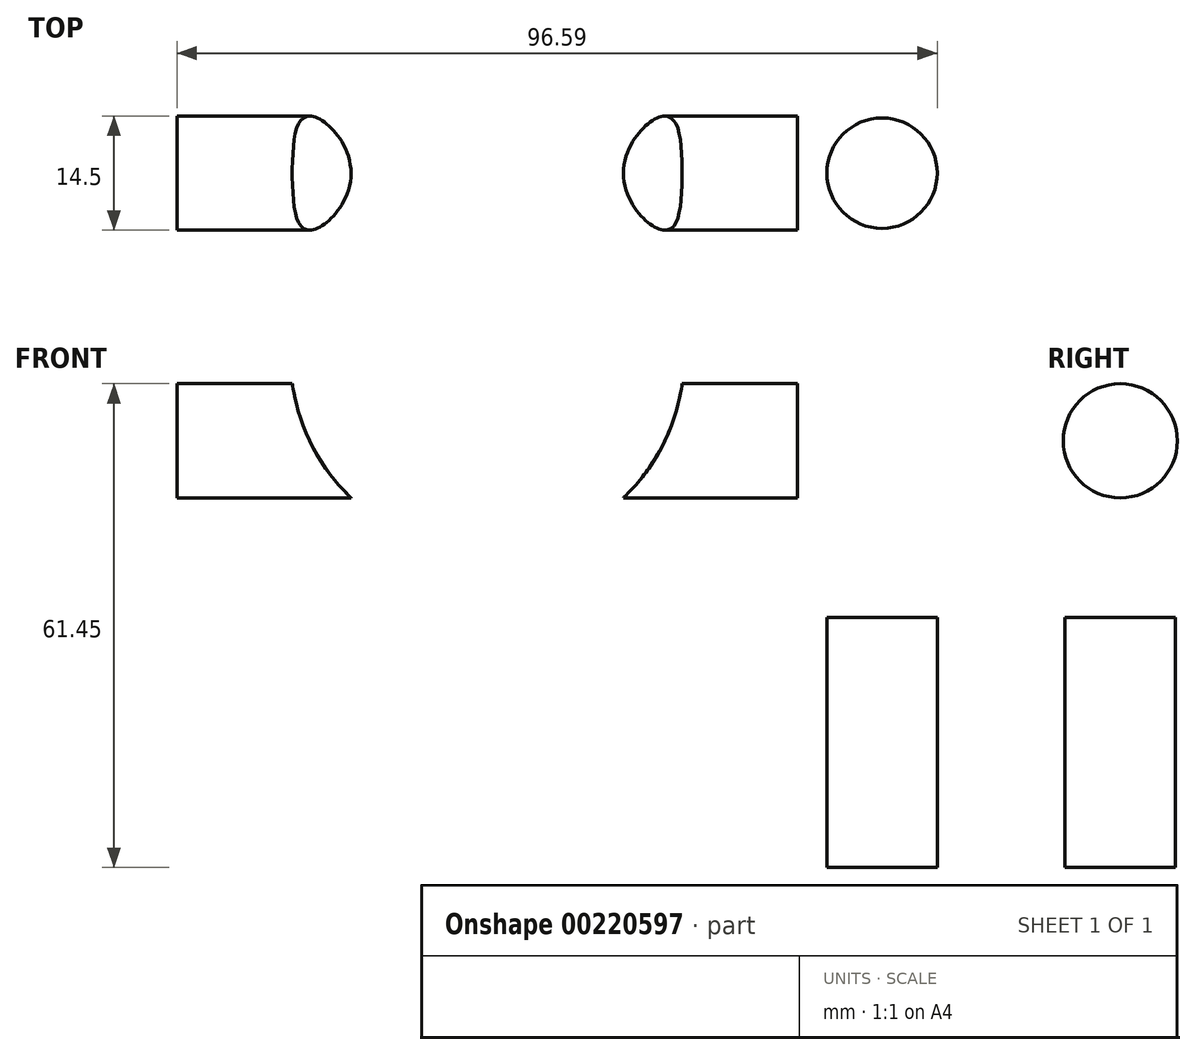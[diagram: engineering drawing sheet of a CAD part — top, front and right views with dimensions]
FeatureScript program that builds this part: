
annotation { "Feature Type Name" : "Feature", "Feature Type Description" : "" }
export const myFeature = defineFeature(function(context is Context, id is Id, definition is map)
    precondition{}
    {
        {
            var Q0;
            Q0=qCreatedBy(makeId("Top.planeOp"),FACE);
            var sketch = newSketch(context, id + "F0", { "sketchPlane" : qUnion([Q0])});
            skLineSegment(sketch, "E0.bottom", {"start": v(-41.16, 20.3) * mm, "end": v(41.16, 20.3) * mm});
            skLineSegment(sketch, "E0.top", {"start": v(-41.16, -20.3) * mm, "end": v(41.16, -20.3) * mm});
            skLineSegment(sketch, "E0.left", {"start": v(-41.16, 20.3) * mm, "end": v(-41.16, -20.3) * mm});
            skLineSegment(sketch, "E0.right", {"start": v(41.16, 20.3) * mm, "end": v(41.16, -20.3) * mm});
            skPoint(sketch, "E0.middle", {"position": v(0, 0) * mm});
            skCircle(sketch, "E1", {"center": v(-41.16, 0) * mm, "radius": 20.36 * mm});
            skCircle(sketch, "E2", {"center": v(41.16, 0) * mm, "radius": 20.35 * mm});
            skSolve(sketch);
        }
        {
            var Q0;
            {var subQ0=sQuery(id+"F0.wireOp",EDGE,"E1");var subQ1=sQuery(id+"F0.wireOp",EDGE,"E0.bottom");var subQ2=makeQuery(id+"F0.imprint","INTERSECT",VERTEX,{"derivedFrom":[subQ1,subQ0]});Q0=makeQuery(id+"F0.imprint","IMPRINT",FACE,{"disambiguationData":[TD([[makeQuery(id+"F0.imprint","IMPRINT",EDGE,{"disambiguationData":[TD([[subQ2,-1.0]])],"derivedFrom":subQ1}),-1.0]])]});}
            var Q1;
            {var subQ0=sQuery(id+"F0.wireOp",EDGE,"E0.left");Q1=makeQuery(id+"F0.imprint","IMPRINT",FACE,{"disambiguationData":[TD([[makeQuery(id+"F0.imprint","IMPRINT",EDGE,{"derivedFrom":subQ0}),1.0]])]});}
            var Q2;
            {var subQ0=sQuery(id+"F0.wireOp",EDGE,"E0.left");Q2=makeQuery(id+"F0.imprint","IMPRINT",FACE,{"disambiguationData":[TD([[makeQuery(id+"F0.imprint","IMPRINT",EDGE,{"derivedFrom":subQ0}),-1.0]])]});}
            var Q3;
            {var subQ0=sQuery(id+"F0.wireOp",EDGE,"E0.right");Q3=makeQuery(id+"F0.imprint","IMPRINT",FACE,{"disambiguationData":[TD([[makeQuery(id+"F0.imprint","IMPRINT",EDGE,{"derivedFrom":subQ0}),-1.0]])]});}
            var Q4;
            {var subQ0=sQuery(id+"F0.wireOp",EDGE,"E0.right");Q4=makeQuery(id+"F0.imprint","IMPRINT",FACE,{"disambiguationData":[TD([[makeQuery(id+"F0.imprint","IMPRINT",EDGE,{"derivedFrom":subQ0}),1.0]])]});}
            extrude(context, id + "F1", {"entities" : qUnion([Q0, Q1, Q2, Q3, Q4]), "depth" : 31.75 * mm});
        }
        {
            var Q0;
            Q0=makeQuery(id+"F1.opExtrude","CAP_FACE",FACE,{"disambiguationData":[OSD([sQuery(id+"F0.wireOp",EDGE,"E0.bottom"),sQuery(id+"F0.wireOp",EDGE,"E0.top"),sQuery(id+"F0.wireOp",EDGE,"E1"),sQuery(id+"F0.wireOp",EDGE,"E2")])],"isStart":false});
            var sketch = newSketch(context, id + "F2", { "sketchPlane" : qUnion([Q0])});
            skCircle(sketch, "E3", {"center": v(-50.15, 0) * mm, "radius": 7.01 * mm});
            skCircle(sketch, "E4.MirrorC", {"center": v(50.15, 0) * mm, "radius": 7.01 * mm});
            skSolve(sketch);
        }
        {
            var Q0;
            Q0=makeQuery(id+"F2.imprint","IMPRINT",FACE,{"disambiguationData":[TD([[makeQuery(id+"F2.imprint","IMPRINT",EDGE,{"derivedFrom":sQuery(id+"F2.wireOp",EDGE,"E4.MirrorC")}),-1.0]])]});
            var Q1;
            Q1=makeQuery(id+"F2.imprint","IMPRINT",FACE,{"disambiguationData":[TD([[makeQuery(id+"F2.imprint","IMPRINT",EDGE,{"derivedFrom":sQuery(id+"F2.wireOp",EDGE,"E3")}),1.0]])]});
            extrude(context, id + "F3", {"entities" : qUnion([Q0, Q1]), "operationType" : NewBodyOperationType.REMOVE, "endBound" : BoundingType.THROUGH_ALL, "oppositeDirection" : true, "depth" : 25.4 * mm});
        }
        {
            var Q0;
            Q0=makeQuery(id+"F1.opExtrude","CAP_FACE",FACE,{"disambiguationData":[OSD([sQuery(id+"F0.wireOp",EDGE,"E0.bottom"),sQuery(id+"F0.wireOp",EDGE,"E0.top"),sQuery(id+"F0.wireOp",EDGE,"E1"),sQuery(id+"F0.wireOp",EDGE,"E2")])],"isStart":false});
            var sketch = newSketch(context, id + "F4", { "sketchPlane" : qUnion([Q0])});
            skLineSegment(sketch, "E5.bottom", {"start": v(-39.43, 13.62) * mm, "end": v(39.43, 13.62) * mm});
            skLineSegment(sketch, "E5.top", {"start": v(-39.43, -13.62) * mm, "end": v(39.43, -13.62) * mm});
            skLineSegment(sketch, "E5.left", {"start": v(-39.43, 13.62) * mm, "end": v(-39.43, -13.62) * mm});
            skLineSegment(sketch, "E5.right", {"start": v(39.43, 13.62) * mm, "end": v(39.43, -13.62) * mm});
            skPoint(sketch, "E5.middle", {"position": v(0, 0) * mm});
            skSolve(sketch);
        }
        {
            var Q0;
            Q0=makeQuery(id+"F4.imprint","IMPRINT",FACE,{"disambiguationData":[TD([[makeQuery(id+"F4.imprint","IMPRINT",EDGE,{"derivedFrom":sQuery(id+"F4.wireOp",EDGE,"E5.bottom")}),-1.0]])]});
            extrude(context, id + "F5", {"entities" : qUnion([Q0]), "operationType" : NewBodyOperationType.ADD, "depth" : 33.27 * mm});
        }
        {
            var Q0;
            Q0=makeQuery(id+"F5.opExtrude","SWEPT_FACE",FACE,{"disambiguationData":[OSD([sQuery(id+"F4.wireOp",EDGE,"E5.top")])]});
            var sketch = newSketch(context, id + "F6", { "sketchPlane" : qUnion([Q0])});
            skCircle(sketch, "E6", {"center": v(0, 65.02) * mm, "radius": 25.02 * mm});
            skSolve(sketch);
        }
        {
            var Q0;
            {var subQ0=sQuery(id+"F6.wireOp",EDGE,"E6");var subQ1=makeQuery(id+"F5.opExtrude","CAP_EDGE",EDGE,{"disambiguationData":[OSD([sQuery(id+"F4.wireOp",EDGE,"E5.top")])],"isStart":false});var subQ2=makeQuery(id+"F6.imprint","INTERSECT",VERTEX,{"disambiguationData":[OD(0.0)],"derivedFrom":[subQ1,subQ0]});Q0=makeQuery(id+"F6.imprint","IMPRINT",FACE,{"disambiguationData":[TD([[makeQuery(id+"F6.imprint","IMPRINT",EDGE,{"disambiguationData":[TD([[subQ2,-1.0]])],"derivedFrom":subQ0}),1.0]])]});}
            extrude(context, id + "F7", {"entities" : qUnion([Q0]), "operationType" : NewBodyOperationType.REMOVE, "endBound" : BoundingType.THROUGH_ALL, "oppositeDirection" : true, "depth" : 25.4 * mm});
        }
        {
            var Q0;
            Q0=makeQuery(id+"F5.opExtrude","SWEPT_FACE",FACE,{"disambiguationData":[OSD([sQuery(id+"F4.wireOp",EDGE,"E5.right")])]});
            var sketch = newSketch(context, id + "F8", { "sketchPlane" : qUnion([Q0])});
            skCircle(sketch, "E7", {"center": v(0, 54.2) * mm, "radius": 7.25 * mm});
            skSolve(sketch);
        }
        {
            var Q0;
            Q0=makeQuery(id+"F8.imprint","IMPRINT",FACE,{"disambiguationData":[TD([[makeQuery(id+"F8.imprint","IMPRINT",EDGE,{"derivedFrom":sQuery(id+"F8.wireOp",EDGE,"E7")}),-1.0]])]});
            extrude(context, id + "F9", {"entities" : qUnion([Q0]), "operationType" : NewBodyOperationType.REMOVE, "oppositeDirection" : true, "depth" : 129.03 * mm});
        }
    });
